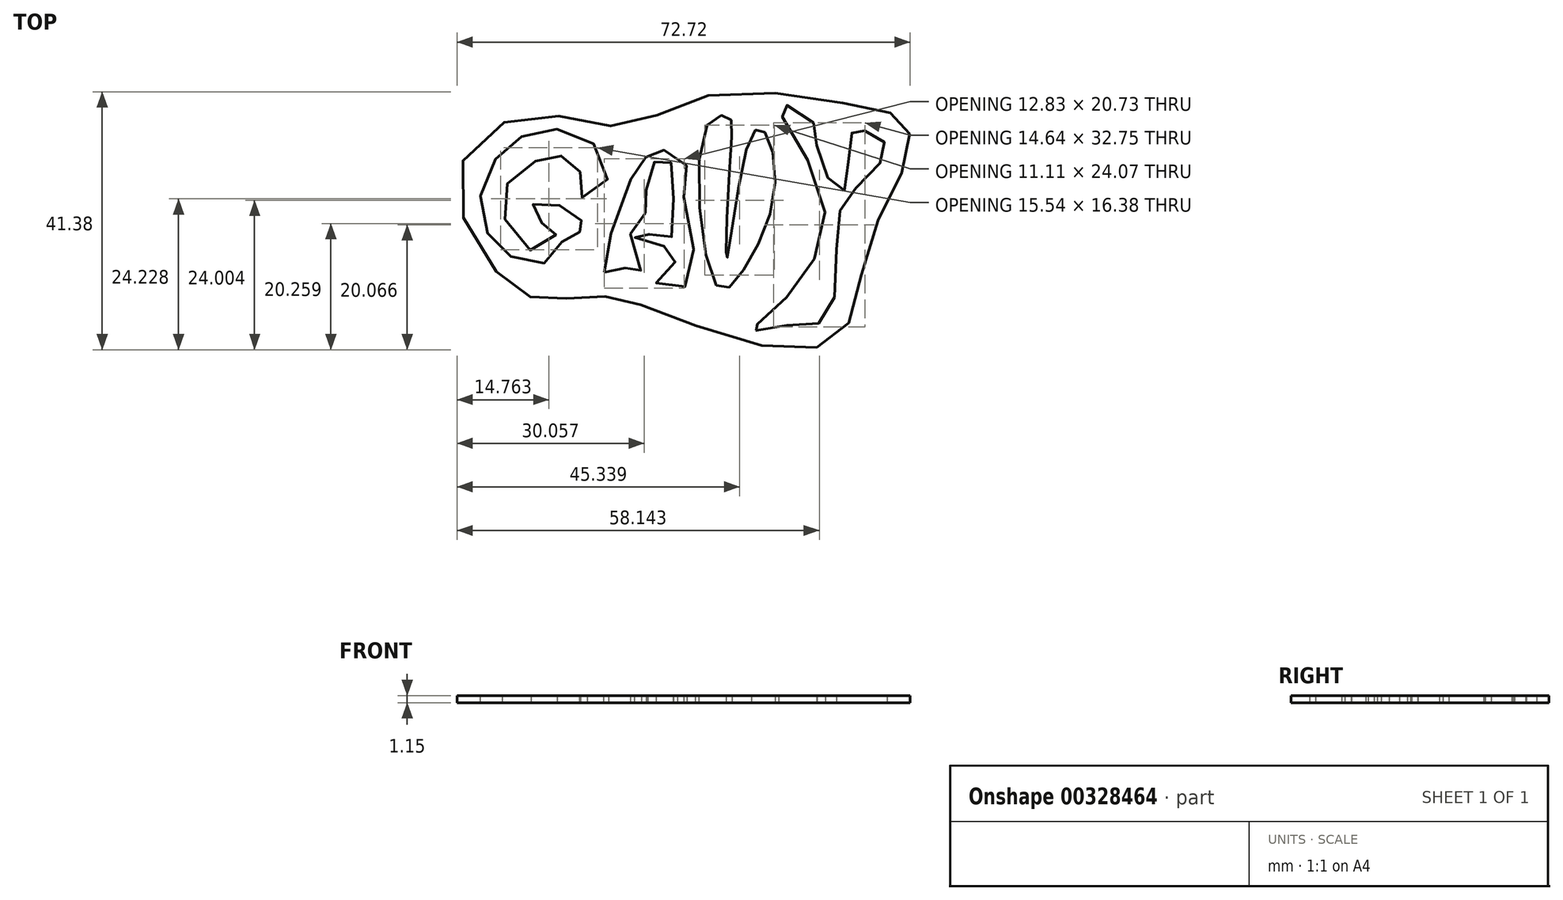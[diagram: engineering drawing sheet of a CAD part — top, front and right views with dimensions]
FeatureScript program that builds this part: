
annotation { "Feature Type Name" : "Feature", "Feature Type Description" : "" }
export const myFeature = defineFeature(function(context is Context, id is Id, definition is map)
    precondition{}
    {
        {
            var Q0;
            Q0=qCreatedBy(makeId("Top.planeOp"),FACE);
            var sketch = newSketch(context, id + "F0", { "sketchPlane" : qUnion([Q0])});
            skFitSpline(sketch, "E0", {"points": [v(209.89, 269.82) * mm, v(198.63, 280.4) * mm, v(184.8, 279.61) * mm, v(160.33, 263.51) * mm, v(159.04, 232.6) * mm, v(182.88, 214.56) * mm, v(193.18, 232.6) * mm, v(179.01, 235.17) * mm, v(177.08, 247.4) * mm, v(194.47, 246.76) * mm, v(208, 239.03) * mm, v(214.44, 226.8) * mm, v(200.91, 229.37) * mm, v(194.47, 211.34) * mm, v(172.57, 206.83) * mm, v(150.03, 219.71) * mm, v(140.1, 249.98) * mm, v(154.53, 283.48) * mm, v(178.37, 297.65) * mm, v(212.5, 294.43) * mm, v(228.66, 264.02) * mm, v(210.57, 252.08) * mm, v(209.89, 269.82) * mm]});
            skFitSpline(sketch, "E1", {"points": [v(226.73, 199.58) * mm, v(243.8, 262) * mm, v(255.63, 280.1) * mm, v(263.35, 285.17) * mm, v(282.9, 276.72) * mm, v(282.25, 252.09) * mm, v(286.2, 191.89) * mm, v(262.98, 191.88) * mm, v(276.89, 208.1) * mm, v(271.94, 216.63) * mm, v(248.15, 223.88) * mm, v(250.08, 228.94) * mm, v(270.35, 221.22) * mm, v(274.8, 247.2) * mm, v(271.75, 278.68) * mm, v(262.39, 277.45) * mm, v(255.87, 255.97) * mm, v(255.87, 241.73) * mm, v(245.01, 227.25) * mm, v(252.25, 198.06) * mm, v(237.05, 203.42) * mm, v(226.73, 199.58) * mm]});
            skFitSpline(sketch, "E2", {"points": [v(372.6, 304.07) * mm, v(348.92, 316.36) * mm, v(378.98, 253.51) * mm, v(352.56, 181.1) * mm, v(329.33, 158.78) * mm, v(350.29, 162.42) * mm, v(382.62, 168.5) * mm, v(389.45, 234.38) * mm, v(403.21, 259.47) * mm, v(424.16, 286.31) * mm, v(412.11, 296.64) * mm, v(401.75, 299.97) * mm, v(397.1, 280.52) * mm, v(392.64, 255.79) * mm, v(375.34, 283.11) * mm, v(372.6, 304.07) * mm]});
            skFitSpline(sketch, "E3", {"points": [v(299.15, 323.08) * mm, v(239.03, 301.67) * mm, v(174.36, 309.41) * mm, v(124.26, 264.78) * mm, v(159.62, 191.63) * mm, v(187.29, 180.76) * mm, v(223.9, 183.02) * mm, v(256.03, 175.56) * mm, v(350.14, 146.3) * mm, v(394.34, 159.57) * mm, v(410.96, 218.6) * mm, v(437.93, 278.85) * mm, v(436.21, 304.68) * mm, v(402.93, 316.15) * mm, v(299.15, 323.08) * mm]});
            skLineSegment(sketch, "E4.bottom", {"start": v(1325.4, 499.43) * mm, "end": v(1425.4, 499.43) * mm});
            skLineSegment(sketch, "E4.top", {"start": v(1325.4, 399.43) * mm, "end": v(1425.4, 399.43) * mm});
            skLineSegment(sketch, "E4.left", {"start": v(1325.4, 499.43) * mm, "end": v(1325.4, 399.43) * mm});
            skLineSegment(sketch, "E4.right", {"start": v(1425.4, 499.43) * mm, "end": v(1425.4, 399.43) * mm});
            skFitSpline(sketch, "E5", {"points": [v(298.32, 302.32) * mm, v(313.15, 308.07) * mm, v(315.34, 292.33) * mm, v(311.94, 208.48) * mm, v(326.47, 287.49) * mm, v(336.32, 299.6) * mm, v(345.84, 259.94) * mm, v(320.72, 196.98) * mm, v(305.89, 189.41) * mm, v(298.32, 302.32) * mm]});
            skSolve(sketch);
        }
        {
            var Q0;
            {var subQ0=sQuery(id+"F0.wireOp",EDGE,"6caU0dwW-yAOF-k51g-r3Lq-jiwAQWNFnLJG");Q0=makeQuery(id+"F0.imprint","IMPRINT",FACE,{"disambiguationData":[TD([[makeQuery(id+"F0.imprint","IMPRINT",EDGE,{"derivedFrom":subQ0}),1.0]])]});}
            var Q1;
            Q1=makeQuery(id+"F0.imprint","IMPRINT",FACE,{"disambiguationData":[TD([[makeQuery(id+"F0.imprint","IMPRINT",EDGE,{"derivedFrom":sQuery(id+"F0.wireOp",EDGE,"E0")}),1.0]])]});
            var Q2;
            {var subQ0=sQuery(id+"F0.wireOp",EDGE,"utrmDivz-IcT1-MuVr-i1Ob-uQS2I2MKeBqC");var subQ1=sQuery(id+"F0.wireOp",EDGE,"ba0bfca1-e8c4-4176-a4ac-38bf1333c8a0");var subQ2=makeQuery(id+"F0.imprint","INTERSECT",VERTEX,{"disambiguationData":[OD(2.0)],"derivedFrom":[subQ1,subQ0]});Q2=makeQuery(id+"F0.imprint","IMPRINT",FACE,{"disambiguationData":[TD([[makeQuery(id+"F0.imprint","IMPRINT",EDGE,{"disambiguationData":[TD([[subQ2,-1.0]])],"derivedFrom":subQ1}),1.0]])]});}
            var Q3;
            {var subQ0=sQuery(id+"F0.wireOp",EDGE,"f5t7qAef-s7kh-IHOZ-vCGn-R2Kg7dUkKzTp");var subQ1=sQuery(id+"F0.wireOp",EDGE,"ba0bfca1-e8c4-4176-a4ac-38bf1333c8a0");var subQ2=makeQuery(id+"F0.imprint","INTERSECT",VERTEX,{"disambiguationData":[OD(2.0)],"derivedFrom":[subQ1,subQ0]});Q3=makeQuery(id+"F0.imprint","IMPRINT",FACE,{"disambiguationData":[TD([[makeQuery(id+"F0.imprint","IMPRINT",EDGE,{"disambiguationData":[TD([[subQ2,-1.0]])],"derivedFrom":subQ1}),1.0]])]});}
            extrude(context, id + "F1", {"entities" : qUnion([Q0, Q1, Q2, Q3]), "depth" : 5 * mm});
        }
        {
            var Q0;
            Q0=qCreatedBy(makeId("Top.planeOp"),FACE);
            var sketch = newSketch(context, id + "F2", { "sketchPlane" : qUnion([Q0])});
            skPoint(sketch, "E6", {"position": v(45.7, 40) * mm});
            skLineSegment(sketch, "E7.bottom", {"start": v(45.7, 40) * mm, "end": v(105.7, 40) * mm});
            skLineSegment(sketch, "E7.top", {"start": v(45.7, 100) * mm, "end": v(105.7, 100) * mm});
            skLineSegment(sketch, "E7.left", {"start": v(45.7, 40) * mm, "end": v(45.7, 100) * mm});
            skLineSegment(sketch, "E7.right", {"start": v(105.7, 40) * mm, "end": v(105.7, 100) * mm});
            skSolve(sketch);
        }
        {
            var Q0;
            Q0=makeQuery(id+"F1.opExtrude","SWEPT_BODY",BODY,{"disambiguationData":[OSD([sQuery(id+"F0.wireOp",EDGE,"E0"),sQuery(id+"F0.wireOp",EDGE,"E1"),sQuery(id+"F0.wireOp",EDGE,"ba0bfca1-e8c4-4176-a4ac-38bf1333c8a0"),sQuery(id+"F0.wireOp",EDGE,"6caU0dwW-yAOF-k51g-r3Lq-jiwAQWNFnLJG"),sQuery(id+"F0.wireOp",EDGE,"A3MEgk3E-FnlT-O8hu-SVDu-ijh4E8NpYx5f"),sQuery(id+"F0.wireOp",EDGE,"E2"),sQuery(id+"F0.wireOp",EDGE,"E3")])]});
            var Q1;
            Q1=sQuery(id+"F2.wireOp",VERTEX,"E6");
            transform(context, id + "F3", {"entities" : qUnion([Q0]), "transformType" : TransformType.SCALE_UNIFORMLY, "scale" : 0.23, "scalePoint" : qUnion([Q1]), "makeCopy" : false});
        }
    });
